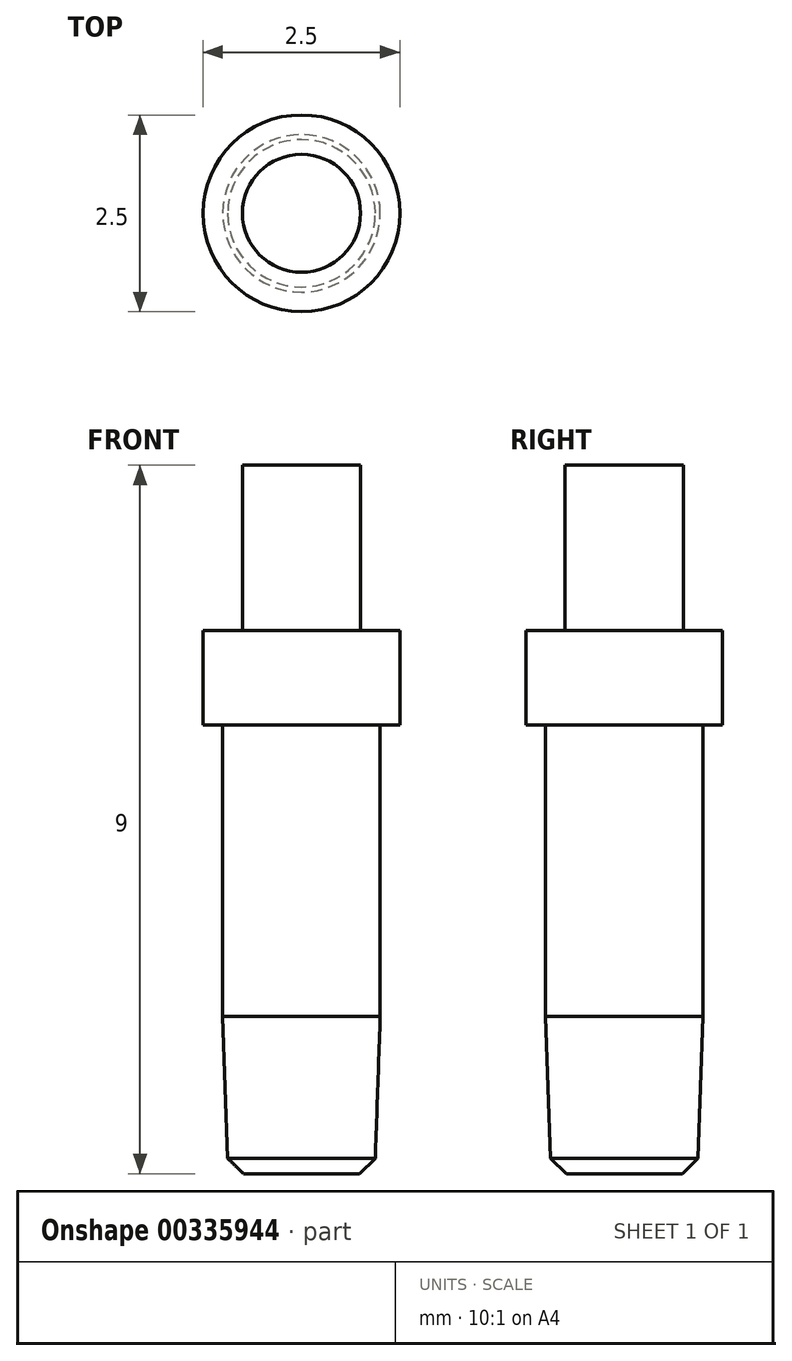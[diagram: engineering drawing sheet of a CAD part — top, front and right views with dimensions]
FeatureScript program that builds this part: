
annotation { "Feature Type Name" : "Feature", "Feature Type Description" : "" }
export const myFeature = defineFeature(function(context is Context, id is Id, definition is map)
    precondition{}
    {
        {
            var Q0;
            Q0=qCreatedBy(makeId("Front.planeOp"),FACE);
            var sketch = newSketch(context, id + "F0", { "sketchPlane" : qUnion([Q0])});
            skLineSegment(sketch, "E0.bottom", {"start": v(-1.25, 0) * mm, "end": v(1.25, 0) * mm});
            skLineSegment(sketch, "E0.top", {"start": v(-1.25, 1.2) * mm, "end": v(1.25, 1.2) * mm});
            skLineSegment(sketch, "E0.left", {"start": v(-1.25, 0) * mm, "end": v(-1.25, 1.2) * mm});
            skLineSegment(sketch, "E0.right", {"start": v(1.25, 0) * mm, "end": v(1.25, 1.2) * mm});
            skLineSegment(sketch, "E1.bottom", {"start": v(-0.75, 1.2) * mm, "end": v(0.75, 1.2) * mm});
            skLineSegment(sketch, "E1.top", {"start": v(-0.75, 3.3) * mm, "end": v(0.75, 3.3) * mm});
            skLineSegment(sketch, "E1.left", {"start": v(-0.75, 1.2) * mm, "end": v(-0.75, 3.3) * mm});
            skLineSegment(sketch, "E1.right", {"start": v(0.75, 1.2) * mm, "end": v(0.75, 3.3) * mm});
            skLineSegment(sketch, "E2.bottom", {"start": v(-1, 0) * mm, "end": v(1, 0) * mm});
            skLineSegment(sketch, "E2.top", {"start": v(-1, -3.7) * mm, "end": v(1, -3.7) * mm});
            skLineSegment(sketch, "E2.left", {"start": v(-1, 0) * mm, "end": v(-1, -3.7) * mm});
            skLineSegment(sketch, "E2.right", {"start": v(1, 0) * mm, "end": v(1, -3.7) * mm});
            skPoint(sketch, "E3", {"position": v(0, 1.2) * mm});
            skLineSegment(sketch, "E4", {"start": v(-1, -3.7) * mm, "end": v(-0.93, -5.7) * mm});
            skLineSegment(sketch, "E5", {"start": v(-0.93, -5.7) * mm, "end": v(0.93, -5.7) * mm});
            skLineSegment(sketch, "E6", {"start": v(0.93, -5.7) * mm, "end": v(1, -3.7) * mm});
            skLineSegment(sketch, "E7", {"start": v(-1, -3.7) * mm, "end": v(-1, -5.7) * mm, "construction": true});
            skLineSegment(sketch, "E8", {"start": v(0, 3.3) * mm, "end": v(0, -5.7) * mm});
            skSolve(sketch);
        }
        {
            var Q0;
            {var subQ0=sQuery(id+"F0.wireOp",EDGE,"E1.left");Q0=makeQuery(id+"F0.imprint","IMPRINT",FACE,{"disambiguationData":[TD([[makeQuery(id+"F0.imprint","IMPRINT",EDGE,{"derivedFrom":subQ0}),-1.0]])]});}
            var Q1;
            {var subQ5=sQuery(id+"F0.wireOp",EDGE,"E0.left");Q1=makeQuery(id+"F0.imprint","IMPRINT",FACE,{"disambiguationData":[TD([[makeQuery(id+"F0.imprint","IMPRINT",EDGE,{"derivedFrom":subQ5}),-1.0]])]});}
            var Q2;
            {var subQ0=sQuery(id+"F0.wireOp",EDGE,"E2.left");Q2=makeQuery(id+"F0.imprint","IMPRINT",FACE,{"disambiguationData":[TD([[makeQuery(id+"F0.imprint","IMPRINT",EDGE,{"derivedFrom":subQ0}),1.0]])]});}
            var Q3;
            {var subQ0=sQuery(id+"F0.wireOp",EDGE,"E4");Q3=makeQuery(id+"F0.imprint","IMPRINT",FACE,{"disambiguationData":[TD([[makeQuery(id+"F0.imprint","IMPRINT",EDGE,{"derivedFrom":subQ0}),1.0]])]});}
            var Q4;
            Q4=sQuery(id+"F0.wireOp",EDGE,"E8");
            revolve(context, id + "F1", {"entities" : qUnion([Q0, Q1, Q2, Q3]), "axis" : qUnion([Q4]), "revolveType" : RevolveType.FULL});
        }
        {
            var Q0;
            Q0=makeQuery(id+"F1.opRevolve","SWEPT_EDGE",EDGE,{"disambiguationData":[OSD([sQuery(id+"F0.wireOp",EDGE,"E4"),sQuery(id+"F0.wireOp",EDGE,"E5")])]});
            chamfer(context, id + "F2", {"entities" : qUnion([Q0]), "width" : 0.2 * mm, "tangentPropagation" : true});
        }
    });
